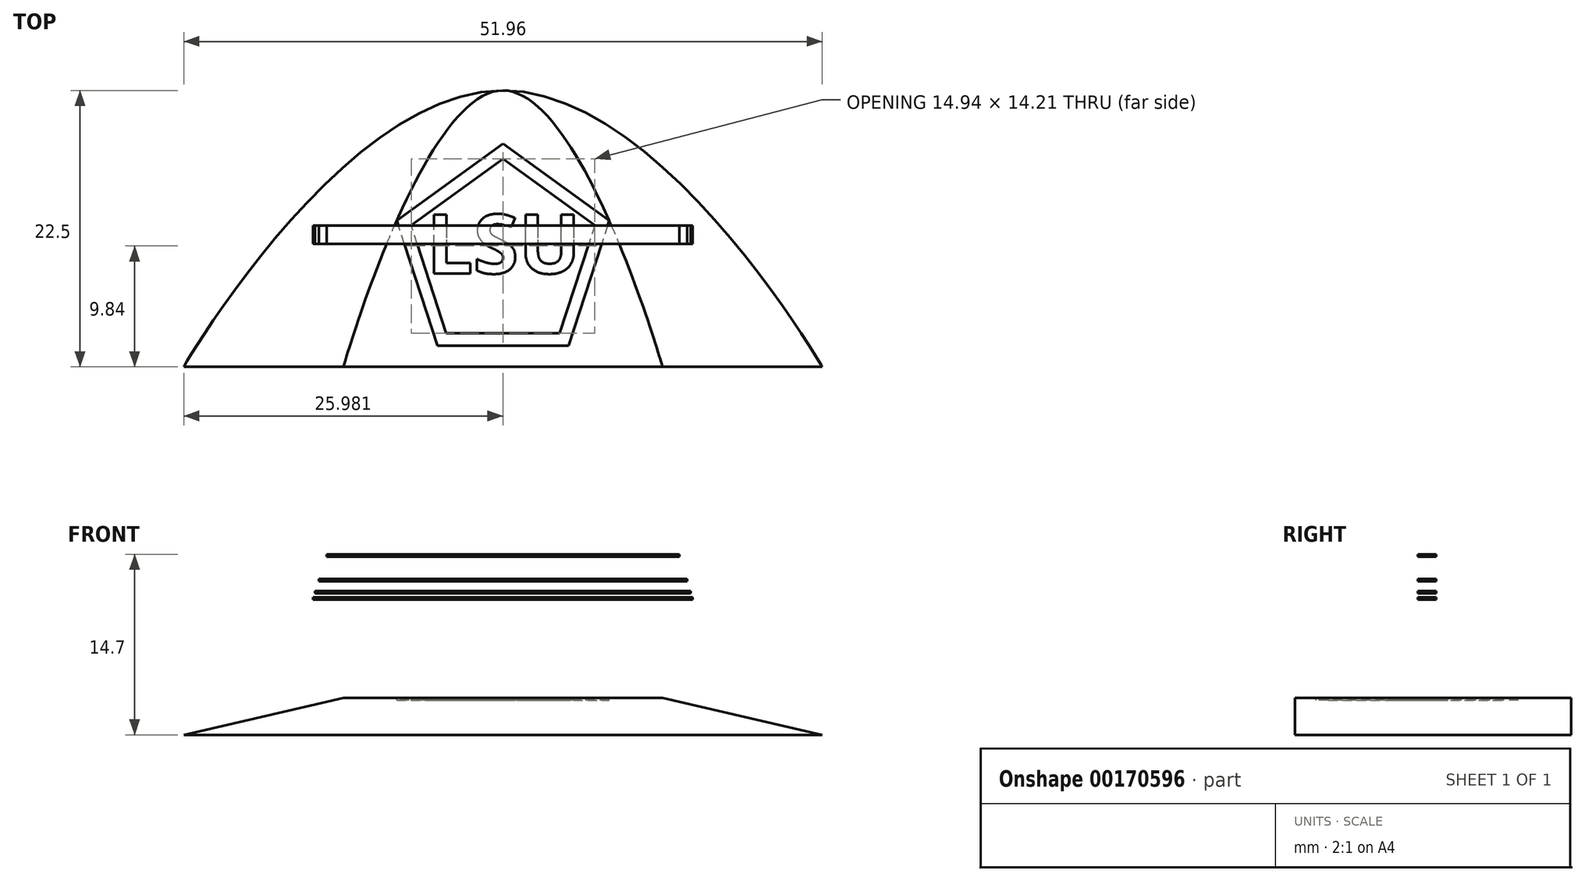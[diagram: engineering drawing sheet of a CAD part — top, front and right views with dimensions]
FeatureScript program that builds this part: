
annotation { "Feature Type Name" : "Feature", "Feature Type Description" : "" }
export const myFeature = defineFeature(function(context is Context, id is Id, definition is map)
    precondition{}
    {
        {
            assignVariable(context, id + "F0", {"name" : "Height", "anyValue" : 2});
        }
        {
            var Q0;
            Q0=qCreatedBy(makeId("Top.planeOp"),FACE);
            var sketch = newSketch(context, id + "F1", { "sketchPlane" : qUnion([Q0])});
            skLineSegment(sketch, "E0", {"start": v(0, 0) * mm, "end": v(34.64, 0) * mm});
            skFitSpline(sketch, "E1", {"points": [v(0, 0) * mm, v(17.32, 15) * mm, v(34.64, 0) * mm], "startDerivative": vector(0, 0.01) * mm, "endDerivative": vector(0, -0.01) * mm});
            skSolve(sketch);
        }
        {
            var Q0;
            Q0=qCreatedBy(makeId("Top.planeOp"),FACE);
            cPlane(context, id + "F2", {"entities" : qUnion([Q0]), "cplaneType" : CPlaneType.OFFSET, "offset" : (getVariable(context, 'Height')) * mm, "width" : 150 * mm, "height" : 150 * mm});
        }
        {
            var Q0;
            Q0=qCreatedBy(id+"F2.planeOp",FACE);
            var sketch = newSketch(context, id + "F3", { "sketchPlane" : qUnion([Q0])});
            skLineSegment(sketch, "E2", {"start": v(8.66, 0) * mm, "end": v(25.98, 0) * mm});
            skFitSpline(sketch, "E3", {"points": [v(8.66, 0) * mm, v(17.32, 15) * mm, v(25.98, 0) * mm], "startDerivative": vector(0, 0.01) * mm, "endDerivative": vector(0, -0.01) * mm});
            skSolve(sketch);
        }
        {
            var Q0;
            Q0=makeQuery(id+"F1.imprint","IMPRINT",FACE,{"disambiguationData":[TD([[makeQuery(id+"F1.imprint","IMPRINT",EDGE,{"derivedFrom":sQuery(id+"F1.wireOp",EDGE,"E0")}),1.0]])]});
            var Q1;
            Q1=qSketchRegion(id+"F3",true);
            loft(context, id + "F4", {"sheetProfilesArray" : [{ "sheetProfileEntities" : qUnion([Q0]) }, { "sheetProfileEntities" : qUnion([Q1]) }]});
        }
        {
            var Q0;
            Q0=makeQuery(id+"F4.opLoft","SWEPT_BODY",BODY,{"disambiguationData":[OSD([makeQuery(id+"F1.imprint","IMPRINT",FACE,{"disambiguationData":[TD([[makeQuery(id+"F1.imprint","IMPRINT",EDGE,{"derivedFrom":sQuery(id+"F1.wireOp",EDGE,"E0")}),1.0]])]}),makeQuery(id+"F3.imprint","IMPRINT",FACE,{"disambiguationData":[TD([[makeQuery(id+"F3.imprint","IMPRINT",EDGE,{"derivedFrom":sQuery(id+"F3.wireOp",EDGE,"E2")}),1.0]])]})])]});
            var Q1;
            Q1=makeQuery(id+"FwXKH3Dz9sJIF4C_1.opExtrude","SWEPT_BODY",BODY,{"disambiguationData":[OSD([sQuery(id+"FOGbtcGzZuJHl9c_1.wireOp",EDGE,"FaClVm9n-j76Q-qotR-Whjm-ICzx4rPetS96.bottom"),sQuery(id+"FOGbtcGzZuJHl9c_1.wireOp",EDGE,"FaClVm9n-j76Q-qotR-Whjm-ICzx4rPetS96.top"),sQuery(id+"FOGbtcGzZuJHl9c_1.wireOp",EDGE,"FaClVm9n-j76Q-qotR-Whjm-ICzx4rPetS96.left"),sQuery(id+"FOGbtcGzZuJHl9c_1.wireOp",EDGE,"FaClVm9n-j76Q-qotR-Whjm-ICzx4rPetS96.right"),sQuery(id+"FOGbtcGzZuJHl9c_1.wireOp",EDGE,"7Pl8r7G1-egdJ-vWa6-5nns-mCmlMner14Cb.top"),sQuery(id+"FOGbtcGzZuJHl9c_1.wireOp",EDGE,"7Pl8r7G1-egdJ-vWa6-5nns-mCmlMner14Cb.left"),sQuery(id+"FOGbtcGzZuJHl9c_1.wireOp",EDGE,"7Pl8r7G1-egdJ-vWa6-5nns-mCmlMner14Cb.right"),sQuery(id+"FOGbtcGzZuJHl9c_1.wireOp",EDGE,"qiKjk8ol-nlLz-KbfR-aYUo-eSb306mj0JBe.bottom"),sQuery(id+"FOGbtcGzZuJHl9c_1.wireOp",EDGE,"qiKjk8ol-nlLz-KbfR-aYUo-eSb306mj0JBe.top"),sQuery(id+"FOGbtcGzZuJHl9c_1.wireOp",EDGE,"qiKjk8ol-nlLz-KbfR-aYUo-eSb306mj0JBe.right")])]});
            var Q2;
            {var subQ0=sQuery(id+"F1.wireOp",EDGE,"E1");var subQ1=sQuery(id+"F1.wireOp",EDGE,"E0");Q2=makeQuery(id+"F4.opLoft","MID_CAP_VERTEX",VERTEX,{"disambiguationData":[OSD([subQ1,subQ0]),TDD([makeQuery(id+"F1.imprint","INTERSECT",VERTEX,{"disambiguationData":[OD(0.0)],"derivedFrom":[subQ1,subQ0]})])],"capPos":0.0});}
            transform(context, id + "F5", {"entities" : qUnion([Q0, Q1]), "transformType" : TransformType.SCALE_UNIFORMLY, "scale" : 1.5, "scalePoint" : qUnion([Q2]), "makeCopy" : false});
        }
        {
            var Q0;
            Q0=makeQuery(id+"F4.opLoft","CAP_FACE",FACE,{"disambiguationData":[OSD([makeQuery(id+"F1.imprint","IMPRINT",FACE,{"disambiguationData":[TD([[makeQuery(id+"F1.imprint","IMPRINT",EDGE,{"derivedFrom":sQuery(id+"F1.wireOp",EDGE,"E0")}),1.0]])]})])],"isStart":true});
            cPlane(context, id + "F6", {"entities" : qUnion([Q0]), "cplaneType" : CPlaneType.OFFSET, "offset" : 12.5 * mm, "oppositeDirection" : true, "width" : 150 * mm, "height" : 150 * mm});
        }
        {
            var Q0;
            Q0=qCreatedBy(id+"F6.planeOp",FACE);
            var sketch = newSketch(context, id + "F7", { "sketchPlane" : qUnion([Q0])});
            skLineSegment(sketch, "E4", {"start": v(46.55, 0) * mm, "end": v(5.41, 0) * mm});
            skFitSpline(sketch, "E5", {"points": [v(5.41, 0) * mm, v(5.41, 0) * mm, v(15.7, -22.5) * mm, v(36.26, -22.5) * mm, v(46.55, 0) * mm, v(46.55, 0) * mm]});
            skLineSegment(sketch, "E6.bottom", {"start": v(11, -11.5) * mm, "end": v(40.96, -11.5) * mm});
            skLineSegment(sketch, "E6.top", {"start": v(11, -10) * mm, "end": v(40.96, -10) * mm});
            skLineSegment(sketch, "E6.left", {"start": v(11, -11.5) * mm, "end": v(11, -10) * mm});
            skLineSegment(sketch, "E6.right", {"start": v(40.96, -11.5) * mm, "end": v(40.96, -10) * mm});
            skSolve(sketch);
        }
        {
            var Q0;
            Q0=qCreatedBy(id+"F6.planeOp",FACE);
            cPlane(context, id + "F8", {"entities" : qUnion([Q0]), "cplaneType" : CPlaneType.OFFSET, "offset" : 1 * mm, "width" : 150 * mm, "height" : 150 * mm});
        }
        {
            var Q0;
            Q0=qCreatedBy(id+"F8.planeOp",FACE);
            var sketch = newSketch(context, id + "F9", { "sketchPlane" : qUnion([Q0])});
            skLineSegment(sketch, "E7", {"start": v(46.98, 0) * mm, "end": v(4.98, 0) * mm});
            skFitSpline(sketch, "E8", {"points": [v(4.98, 0) * mm, v(4.98, 0) * mm, v(15.48, -22.5) * mm, v(36.48, -22.5) * mm, v(46.98, 0) * mm, v(46.98, 0) * mm]});
            skLineSegment(sketch, "E9.bottom", {"start": v(10.69, -10) * mm, "end": v(41.27, -10) * mm});
            skLineSegment(sketch, "E9.top", {"start": v(10.69, -11.5) * mm, "end": v(41.27, -11.5) * mm});
            skLineSegment(sketch, "E9.left", {"start": v(10.69, -10) * mm, "end": v(10.69, -11.5) * mm});
            skLineSegment(sketch, "E9.right", {"start": v(41.27, -10) * mm, "end": v(41.27, -11.5) * mm});
            skSolve(sketch);
        }
        {
            var Q0;
            Q0=qCreatedBy(id+"F8.planeOp",FACE);
            cPlane(context, id + "F10", {"entities" : qUnion([Q0]), "cplaneType" : CPlaneType.OFFSET, "offset" : .5 * mm, "width" : 150 * mm, "height" : 150 * mm});
        }
        {
            var Q0;
            Q0=qCreatedBy(id+"F10.planeOp",FACE);
            var sketch = newSketch(context, id + "F11", { "sketchPlane" : qUnion([Q0])});
            skFitSpline(sketch, "E10", {"points": [v(4.76, 0) * mm, v(4.76, 0) * mm, v(15.37, -22.5) * mm, v(36.59, -22.5) * mm, v(47.2, 0) * mm, v(47.2, 0) * mm]});
            skLineSegment(sketch, "E11", {"start": v(47.2, 0) * mm, "end": v(4.76, 0) * mm});
            skLineSegment(sketch, "E12.bottom", {"start": v(10.53, -10) * mm, "end": v(41.43, -10) * mm});
            skLineSegment(sketch, "E12.top", {"start": v(10.53, -11.5) * mm, "end": v(41.43, -11.5) * mm});
            skLineSegment(sketch, "E12.left", {"start": v(10.53, -10) * mm, "end": v(10.53, -11.5) * mm});
            skLineSegment(sketch, "E12.right", {"start": v(41.43, -10) * mm, "end": v(41.43, -11.5) * mm});
            skSolve(sketch);
        }
        {
            var Q0;
            {var subQ0=sQuery(id+"F7.wireOp",EDGE,"E6.top");Q0=makeQuery(id+"F7.imprint","IMPRINT",FACE,{"disambiguationData":[TD([[makeQuery(id+"F7.imprint","IMPRINT",EDGE,{"derivedFrom":subQ0}),-1.0]])]});}
            extrude(context, id + "F12", {"entities" : qUnion([Q0]), "operationType" : NewBodyOperationType.REMOVE, "oppositeDirection" : true, "depth" : .2 * mm});
        }
        {
            var Q0;
            {var subQ0=sQuery(id+"F9.wireOp",EDGE,"E9.bottom");Q0=makeQuery(id+"F9.imprint","IMPRINT",FACE,{"disambiguationData":[TD([[makeQuery(id+"F9.imprint","IMPRINT",EDGE,{"derivedFrom":subQ0}),-1.0]])]});}
            extrude(context, id + "F13", {"entities" : qUnion([Q0]), "operationType" : NewBodyOperationType.REMOVE, "oppositeDirection" : true, "depth" : .2 * mm});
        }
        {
            var Q0;
            {var subQ0=sQuery(id+"F11.wireOp",EDGE,"E12.bottom");Q0=makeQuery(id+"F11.imprint","IMPRINT",FACE,{"disambiguationData":[TD([[makeQuery(id+"F11.imprint","IMPRINT",EDGE,{"derivedFrom":subQ0}),-1.0]])]});}
            extrude(context, id + "F14", {"entities" : qUnion([Q0]), "operationType" : NewBodyOperationType.REMOVE, "oppositeDirection" : true, "depth" : .2 * mm});
        }
        {
            var Q0;
            {var subQ0=sQuery(id+"F7.wireOp",EDGE,"E6.top");Q0=makeQuery(id+"F7.imprint","IMPRINT",FACE,{"disambiguationData":[TD([[makeQuery(id+"F7.imprint","IMPRINT",EDGE,{"derivedFrom":subQ0}),-1.0]])]});}
            extrude(context, id + "F15", {"entities" : qUnion([Q0]), "oppositeDirection" : true, "depth" : .2 * mm});
        }
        {
            var Q0;
            {var subQ0=sQuery(id+"F9.wireOp",EDGE,"E9.bottom");Q0=makeQuery(id+"F9.imprint","IMPRINT",FACE,{"disambiguationData":[TD([[makeQuery(id+"F9.imprint","IMPRINT",EDGE,{"derivedFrom":subQ0}),-1.0]])]});}
            extrude(context, id + "F16", {"entities" : qUnion([Q0]), "oppositeDirection" : true, "depth" : .2 * mm});
        }
        {
            var Q0;
            {var subQ0=sQuery(id+"F11.wireOp",EDGE,"E12.bottom");Q0=makeQuery(id+"F11.imprint","IMPRINT",FACE,{"disambiguationData":[TD([[makeQuery(id+"F11.imprint","IMPRINT",EDGE,{"derivedFrom":subQ0}),-1.0]])]});}
            extrude(context, id + "F17", {"entities" : qUnion([Q0]), "oppositeDirection" : true, "depth" : .2 * mm});
        }
        {
            var Q0;
            Q0=qCreatedBy(id+"F6.planeOp",FACE);
            cPlane(context, id + "F18", {"entities" : qUnion([Q0]), "cplaneType" : CPlaneType.OFFSET, "offset" : 2 * mm, "oppositeDirection" : true, "width" : 150 * mm, "height" : 150 * mm});
        }
        {
            var Q0;
            Q0=qCreatedBy(id+"F18.planeOp",FACE);
            var sketch = newSketch(context, id + "F19", { "sketchPlane" : qUnion([Q0])});
            skFitSpline(sketch, "E13", {"points": [v(6.28, 0) * mm, v(6.28, 0) * mm, v(16.13, -22.5) * mm, v(35.83, -22.5) * mm, v(45.68, 0) * mm, v(45.68, 0) * mm]});
            skLineSegment(sketch, "E14", {"start": v(45.68, 0) * mm, "end": v(6.28, 0) * mm});
            skLineSegment(sketch, "E15.bottom", {"start": v(11.63, -10) * mm, "end": v(40.33, -10) * mm});
            skLineSegment(sketch, "E15.top", {"start": v(11.63, -11.5) * mm, "end": v(40.33, -11.5) * mm});
            skLineSegment(sketch, "E15.left", {"start": v(11.63, -10) * mm, "end": v(11.63, -11.5) * mm});
            skLineSegment(sketch, "E15.right", {"start": v(40.33, -10) * mm, "end": v(40.33, -11.5) * mm});
            skSolve(sketch);
        }
        {
            var Q0;
            {var subQ0=sQuery(id+"F19.wireOp",EDGE,"E15.bottom");Q0=makeQuery(id+"F19.imprint","IMPRINT",FACE,{"disambiguationData":[TD([[makeQuery(id+"F19.imprint","IMPRINT",EDGE,{"derivedFrom":subQ0}),-1.0]])]});}
            extrude(context, id + "F20", {"entities" : qUnion([Q0]), "operationType" : NewBodyOperationType.REMOVE, "oppositeDirection" : true, "depth" : .2 * mm});
        }
        {
            var Q0;
            {var subQ0=sQuery(id+"F19.wireOp",EDGE,"E15.bottom");Q0=makeQuery(id+"F19.imprint","IMPRINT",FACE,{"disambiguationData":[TD([[makeQuery(id+"F19.imprint","IMPRINT",EDGE,{"derivedFrom":subQ0}),-1.0]])]});}
            extrude(context, id + "F21", {"entities" : qUnion([Q0]), "oppositeDirection" : true, "depth" : .2 * mm});
        }
        {
            var Q0;
            Q0=makeQuery(id+"F4.opLoft","CAP_FACE",FACE,{"disambiguationData":[OSD([makeQuery(id+"F3.imprint","IMPRINT",FACE,{"disambiguationData":[TD([[makeQuery(id+"F3.imprint","IMPRINT",EDGE,{"derivedFrom":sQuery(id+"F3.wireOp",EDGE,"E2")}),1.0]])]})])],"isStart":true});
            var sketch = newSketch(context, id + "F22", { "sketchPlane" : qUnion([Q0])});
            skCircle(sketch, "E16.cCircle", {"center": v(25.98, 9.1) * mm, "radius": 9.1 * mm, "construction": true});
            skPoint(sketch, "E16.cCircle.centerSnap0", {"position": v(25.98, 0) * mm});
            skLineSegment(sketch, "E16.0", {"start": v(34.63, 11.9) * mm, "end": v(31.32, 1.74) * mm});
            skLineSegment(sketch, "E16.1", {"start": v(31.32, 1.74) * mm, "end": v(20.64, 1.74) * mm});
            skLineSegment(sketch, "E16.2", {"start": v(20.64, 1.74) * mm, "end": v(17.34, 11.9) * mm});
            skLineSegment(sketch, "E16.3", {"start": v(17.34, 11.9) * mm, "end": v(25.98, 18.18) * mm});
            skLineSegment(sketch, "E16.4", {"start": v(25.98, 18.18) * mm, "end": v(34.63, 11.9) * mm});
            skLineSegment(sketch, "E17.0", {"start": v(18.51, 11.52) * mm, "end": v(25.98, 16.94) * mm});
            skLineSegment(sketch, "E17.1", {"start": v(21.36, 2.74) * mm, "end": v(18.51, 11.52) * mm});
            skLineSegment(sketch, "E17.2", {"start": v(25.98, 16.94) * mm, "end": v(33.45, 11.52) * mm});
            skLineSegment(sketch, "E17.3", {"start": v(33.45, 11.52) * mm, "end": v(30.6, 2.74) * mm});
            skLineSegment(sketch, "E17.4", {"start": v(30.6, 2.74) * mm, "end": v(21.36, 2.74) * mm});
            skText(sketch, "E18", { "text": "LSU", "fontName": "OpenSans-Bold.ttf"});
            const initialGuessF22  = {"E18": [0.01978, 0.00761, 1, 0, 0.00482]};
            skSetInitialGuess(sketch, initialGuessF22);
            skSolve(sketch);
        }
        {
            var Q0;
            Q0=makeQuery(id+"F22.imprint","IMPRINT",FACE,{"disambiguationData":[TD([[makeQuery(id+"F22.imprint","IMPRINT",EDGE,{"derivedFrom":sQuery(id+"F22.wireOp",EDGE,"E18.sketch_text.stroke-6")}),-1.0]])]});
            var Q1;
            Q1=makeQuery(id+"F22.imprint","IMPRINT",FACE,{"disambiguationData":[TD([[makeQuery(id+"F22.imprint","IMPRINT",EDGE,{"derivedFrom":sQuery(id+"F22.wireOp",EDGE,"E18.sketch_text.stroke-34")}),-1.0]])]});
            var Q2;
            Q2=makeQuery(id+"F22.imprint","IMPRINT",FACE,{"disambiguationData":[TD([[makeQuery(id+"F22.imprint","IMPRINT",EDGE,{"derivedFrom":sQuery(id+"F22.wireOp",EDGE,"E18.sketch_text.stroke-0")}),-1.0]])]});
            var Q3;
            Q3=makeQuery(id+"F22.imprint","IMPRINT",FACE,{"disambiguationData":[TD([[makeQuery(id+"F22.imprint","IMPRINT",EDGE,{"derivedFrom":sQuery(id+"F22.wireOp",EDGE,"E16.0")}),-1.0]])]});
            extrude(context, id + "F23", {"entities" : qUnion([Q0, Q1, Q2, Q3]), "operationType" : NewBodyOperationType.REMOVE, "oppositeDirection" : true, "depth" : .2 * mm});
        }
        {
            var Q0;
            Q0=makeQuery(id+"F22.imprint","IMPRINT",FACE,{"disambiguationData":[TD([[makeQuery(id+"F22.imprint","IMPRINT",EDGE,{"derivedFrom":sQuery(id+"F22.wireOp",EDGE,"E18.sketch_text.stroke-0")}),-1.0]])]});
            var Q1;
            Q1=makeQuery(id+"F22.imprint","IMPRINT",FACE,{"disambiguationData":[TD([[makeQuery(id+"F22.imprint","IMPRINT",EDGE,{"derivedFrom":sQuery(id+"F22.wireOp",EDGE,"E18.sketch_text.stroke-6")}),-1.0]])]});
            var Q2;
            Q2=makeQuery(id+"F22.imprint","IMPRINT",FACE,{"disambiguationData":[TD([[makeQuery(id+"F22.imprint","IMPRINT",EDGE,{"derivedFrom":sQuery(id+"F22.wireOp",EDGE,"E18.sketch_text.stroke-34")}),-1.0]])]});
            var Q3;
            Q3=makeQuery(id+"F22.imprint","IMPRINT",FACE,{"disambiguationData":[TD([[makeQuery(id+"F22.imprint","IMPRINT",EDGE,{"derivedFrom":sQuery(id+"F22.wireOp",EDGE,"E16.0")}),-1.0]])]});
            extrude(context, id + "F24", {"entities" : qUnion([Q0, Q1, Q2, Q3]), "oppositeDirection" : true, "depth" : .2 * mm});
        }
    });
